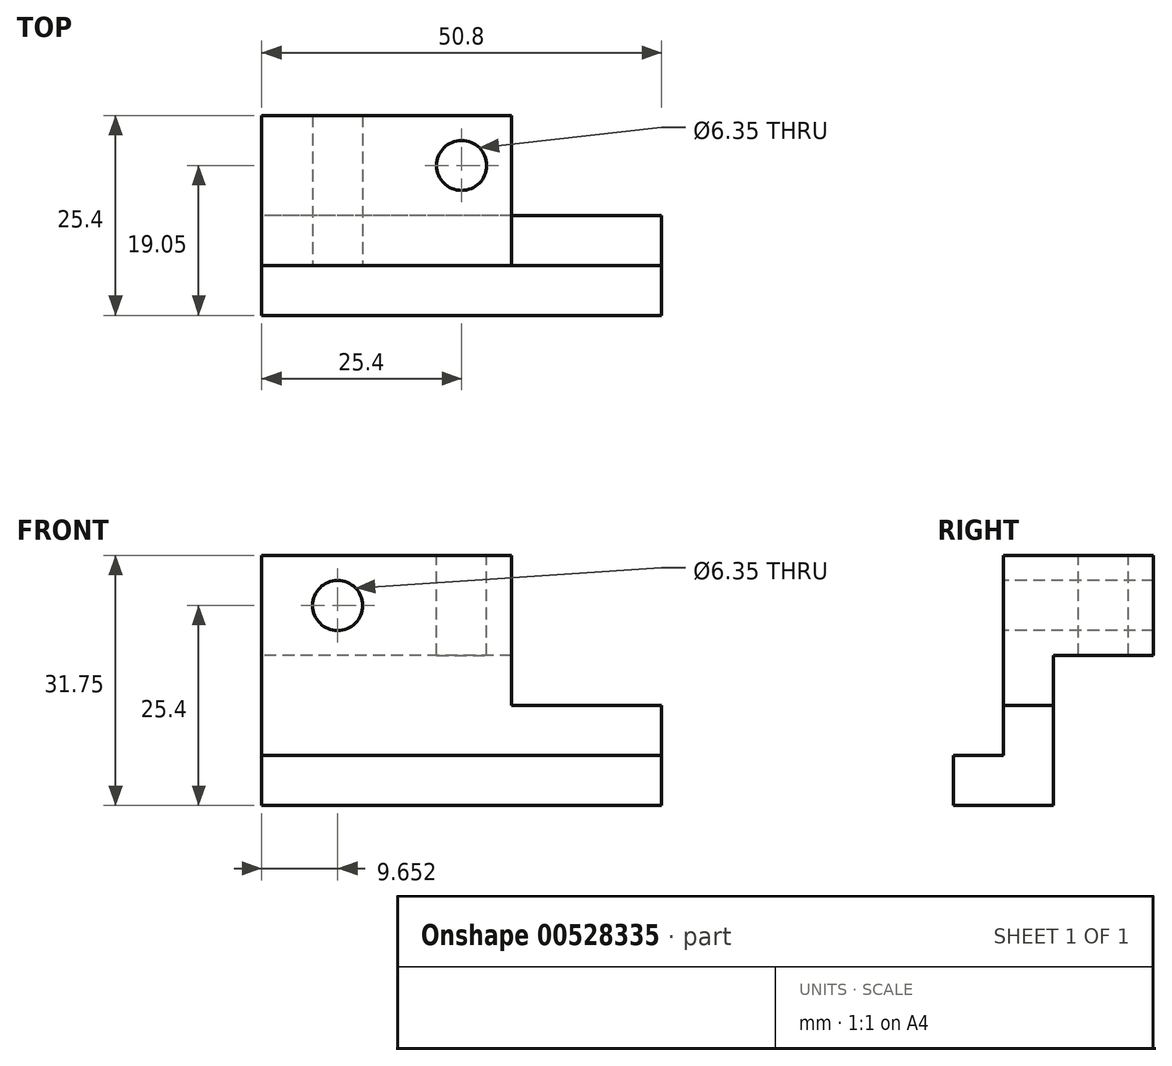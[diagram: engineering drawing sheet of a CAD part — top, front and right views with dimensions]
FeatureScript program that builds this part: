
annotation { "Feature Type Name" : "Feature", "Feature Type Description" : "" }
export const myFeature = defineFeature(function(context is Context, id is Id, definition is map)
    precondition{}
    {
        {
            var Q0;
            Q0=qCreatedBy(makeId("Right.planeOp"),FACE);
            var sketch = newSketch(context, id + "F0", { "sketchPlane" : qUnion([Q0])});
            skLineSegment(sketch, "E0", {"start": v(0, 0) * mm, "end": v(0, -12.7) * mm});
            skLineSegment(sketch, "E1", {"start": v(0, -12.7) * mm, "end": v(-12.7, -12.7) * mm});
            skLineSegment(sketch, "E2", {"start": v(-12.7, -12.7) * mm, "end": v(-12.7, -19.05) * mm});
            skLineSegment(sketch, "E3", {"start": v(-12.7, -19.05) * mm, "end": v(-19.05, -19.05) * mm});
            skLineSegment(sketch, "E4", {"start": v(-19.05, -19.05) * mm, "end": v(-19.05, 0) * mm});
            skLineSegment(sketch, "E5", {"start": v(-19.05, 0) * mm, "end": v(0, 0) * mm});
            skLineSegment(sketch, "E6", {"start": v(-12.7, -19.05) * mm, "end": v(-12.7, -31.75) * mm});
            skLineSegment(sketch, "E7", {"start": v(-12.7, -31.75) * mm, "end": v(-25.4, -31.75) * mm});
            skLineSegment(sketch, "E8", {"start": v(-25.4, -31.75) * mm, "end": v(-25.4, -25.4) * mm});
            skLineSegment(sketch, "E9", {"start": v(-25.4, -25.4) * mm, "end": v(-19.05, -25.4) * mm});
            skLineSegment(sketch, "E10", {"start": v(-19.05, -25.4) * mm, "end": v(-19.05, -19.05) * mm});
            skSolve(sketch);
        }
        {
            var Q0;
            Q0=makeQuery(id+"F0.imprint","IMPRINT",FACE,{"disambiguationData":[TD([[makeQuery(id+"F0.imprint","IMPRINT",EDGE,{"derivedFrom":sQuery(id+"F0.wireOp",EDGE,"E0")}),-1.0]])]});
            extrude(context, id + "F1", {"entities" : qUnion([Q0]), "depth" : 31.75 * mm, "offsetDistance" : 25.4 * mm});
        }
        {
            var Q0;
            Q0=makeQuery(id+"F0.imprint","IMPRINT",FACE,{"disambiguationData":[TD([[makeQuery(id+"F0.imprint","IMPRINT",EDGE,{"derivedFrom":sQuery(id+"F0.wireOp",EDGE,"E3")}),1.0]])]});
            extrude(context, id + "F2", {"entities" : qUnion([Q0]), "operationType" : NewBodyOperationType.ADD, "depth" : 50.8 * mm, "offsetDistance" : 25.4 * mm});
        }
        {
            var Q0;
            Q0=makeQuery(id+"F2.boolean.opBoolean","MERGE",FACE,{"derivedFrom":[makeQuery(id+"F1.opExtrude","SWEPT_FACE",FACE,{"disambiguationData":[OSD([sQuery(id+"F0.wireOp",EDGE,"E4")])]}),makeQuery(id+"F2.opExtrude","SWEPT_FACE",FACE,{"disambiguationData":[OSD([sQuery(id+"F0.wireOp",EDGE,"E10")])]})]});
            var sketch = newSketch(context, id + "F3", { "sketchPlane" : qUnion([Q0])});
            skLineSegment(sketch, "E11", {"start": v(0, 0) * mm, "end": v(9.65, 0) * mm, "construction": true});
            skLineSegment(sketch, "E12", {"start": v(9.65, 0) * mm, "end": v(9.65, -6.35) * mm, "construction": true});
            skCircle(sketch, "E13", {"center": v(9.65, -6.35) * mm, "radius": 3.18 * mm});
            skSolve(sketch);
        }
        {
            var Q0;
            Q0 = qSketchRegion(id + "F3", true);
            extrude(context, id + "F4", {"entities" : qUnion([Q0]), "operationType" : NewBodyOperationType.REMOVE, "endBound" : BoundingType.THROUGH_ALL, "oppositeDirection" : true, "depth" : 25.4 * mm, "offsetDistance" : 25.4 * mm});
        }
        {
            var Q0;
            Q0=makeQuery(id+"F1.opExtrude","SWEPT_FACE",FACE,{"disambiguationData":[OSD([sQuery(id+"F0.wireOp",EDGE,"E5")])]});
            var sketch = newSketch(context, id + "F5", { "sketchPlane" : qUnion([Q0])});
            skLineSegment(sketch, "E14", {"start": v(31.75, 0) * mm, "end": v(25.4, 0) * mm, "construction": true});
            skLineSegment(sketch, "E15", {"start": v(25.4, 0) * mm, "end": v(25.4, -6.35) * mm, "construction": true});
            skCircle(sketch, "E16", {"center": v(25.4, -6.35) * mm, "radius": 3.18 * mm});
            skSolve(sketch);
        }
        {
            var Q0;
            Q0 = qSketchRegion(id + "F5", true);
            extrude(context, id + "F6", {"entities" : qUnion([Q0]), "operationType" : NewBodyOperationType.REMOVE, "endBound" : BoundingType.THROUGH_ALL, "oppositeDirection" : true, "depth" : 25.4 * mm, "offsetDistance" : 25.4 * mm});
        }
    });
